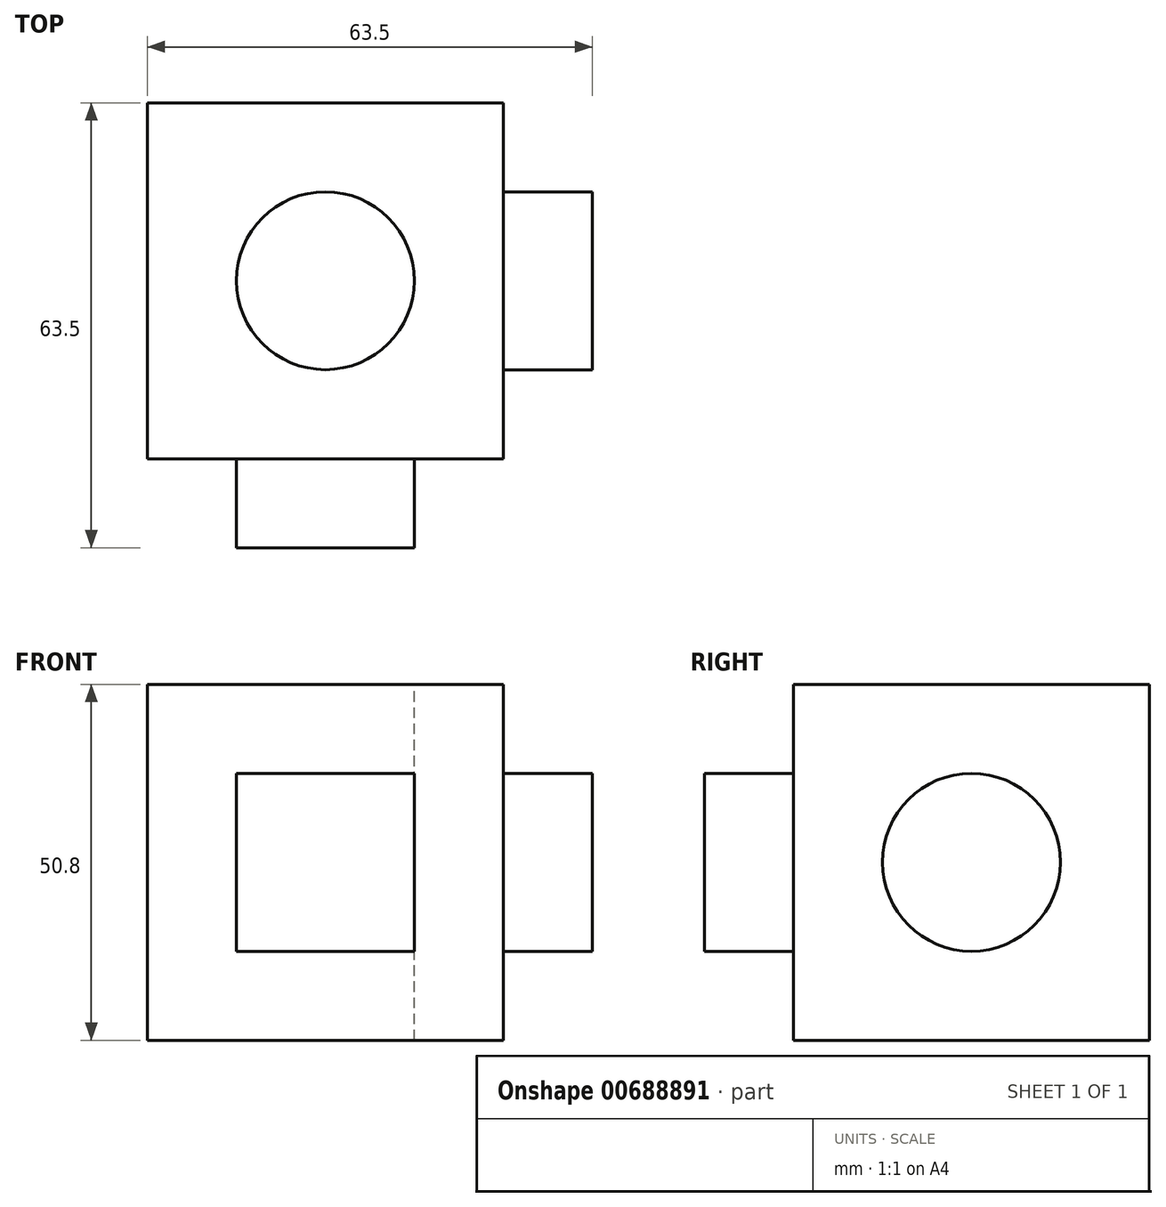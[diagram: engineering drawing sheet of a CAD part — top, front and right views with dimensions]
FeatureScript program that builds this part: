
annotation { "Feature Type Name" : "Feature", "Feature Type Description" : "" }
export const myFeature = defineFeature(function(context is Context, id is Id, definition is map)
    precondition{}
    {
        {
            var Q0;
            Q0=qCreatedBy(makeId("Front.planeOp"),FACE);
            var sketch = newSketch(context, id + "F0", { "sketchPlane" : qUnion([Q0])});
            skLineSegment(sketch, "E0", {"start": v(0, 0) * mm, "end": v(-50.8, 0) * mm});
            skLineSegment(sketch, "E1", {"start": v(-50.8, 0) * mm, "end": v(-50.8, 50.8) * mm});
            skLineSegment(sketch, "E2", {"start": v(-50.8, 50.8) * mm, "end": v(0, 50.8) * mm});
            skLineSegment(sketch, "E3", {"start": v(0, 50.8) * mm, "end": v(0, 0) * mm});
            skSolve(sketch);
        }
        {
            var Q0;
            Q0=makeQuery(id+"F0.imprint","IMPRINT",FACE,{"disambiguationData":[TD([[makeQuery(id+"F0.imprint","IMPRINT",EDGE,{"derivedFrom":sQuery(id+"F0.wireOp",EDGE,"E0")}),-1.0]])]});
            extrude(context, id + "F1", {"entities" : qUnion([Q0]), "depth" : 50.8 * mm, "offsetDistance" : 25.4 * mm});
        }
        {
            var Q0;
            Q0=makeQuery(id+"F1.opExtrude","SWEPT_FACE",FACE,{"disambiguationData":[OSD([sQuery(id+"F0.wireOp",EDGE,"E2")])]});
            var sketch = newSketch(context, id + "F2", { "sketchPlane" : qUnion([Q0])});
            skCircle(sketch, "E4", {"center": v(-25.4, -25.4) * mm, "radius": 12.7 * mm});
            skSolve(sketch);
        }
        {
            var Q0;
            Q0=makeQuery(id+"F2.imprint","IMPRINT",FACE,{"disambiguationData":[TD([[makeQuery(id+"F2.imprint","IMPRINT",EDGE,{"derivedFrom":sQuery(id+"F2.wireOp",EDGE,"E4")}),1.0]])]});
            extrude(context, id + "F3", {"entities" : qUnion([Q0]), "operationType" : NewBodyOperationType.REMOVE, "oppositeDirection" : true, "depth" : 50.8 * mm, "offsetDistance" : 25.4 * mm});
        }
        {
            var Q0;
            Q0=makeQuery(id+"F1.opExtrude","CAP_FACE",FACE,{"disambiguationData":[OSD([sQuery(id+"F0.wireOp",EDGE,"E0"),sQuery(id+"F0.wireOp",EDGE,"E1"),sQuery(id+"F0.wireOp",EDGE,"E2"),sQuery(id+"F0.wireOp",EDGE,"E3")])],"isStart":false});
            var sketch = newSketch(context, id + "F4", { "sketchPlane" : qUnion([Q0])});
            skLineSegment(sketch, "E5.bottom", {"start": v(-12.7, 38.1) * mm, "end": v(-38.1, 38.1) * mm});
            skLineSegment(sketch, "E5.top", {"start": v(-12.7, 12.7) * mm, "end": v(-38.1, 12.7) * mm});
            skLineSegment(sketch, "E5.left", {"start": v(-12.7, 38.1) * mm, "end": v(-12.7, 12.7) * mm});
            skLineSegment(sketch, "E5.right", {"start": v(-38.1, 38.1) * mm, "end": v(-38.1, 12.7) * mm});
            skPoint(sketch, "E5.middle", {"position": v(-25.4, 25.4) * mm});
            skSolve(sketch);
        }
        {
            var Q0;
            Q0=makeQuery(id+"F4.imprint","IMPRINT",FACE,{"disambiguationData":[TD([[makeQuery(id+"F4.imprint","IMPRINT",EDGE,{"derivedFrom":sQuery(id+"F4.wireOp",EDGE,"E5.bottom")}),1.0]])]});
            extrude(context, id + "F5", {"entities" : qUnion([Q0]), "operationType" : NewBodyOperationType.ADD, "depth" : 12.7 * mm, "offsetDistance" : 25.4 * mm});
        }
        {
            var Q0;
            Q0=makeQuery(id+"F1.opExtrude","SWEPT_FACE",FACE,{"disambiguationData":[OSD([sQuery(id+"F0.wireOp",EDGE,"E3")])]});
            var sketch = newSketch(context, id + "F6", { "sketchPlane" : qUnion([Q0])});
            skCircle(sketch, "E6", {"center": v(-25.4, 25.4) * mm, "radius": 12.7 * mm});
            skSolve(sketch);
        }
        {
            var Q0;
            Q0=makeQuery(id+"F6.imprint","IMPRINT",FACE,{"disambiguationData":[TD([[makeQuery(id+"F6.imprint","IMPRINT",EDGE,{"derivedFrom":sQuery(id+"F6.wireOp",EDGE,"E6")}),1.0]])]});
            extrude(context, id + "F7", {"entities" : qUnion([Q0]), "operationType" : NewBodyOperationType.ADD, "depth" : 12.7 * mm, "offsetDistance" : 25.4 * mm});
        }
    });
